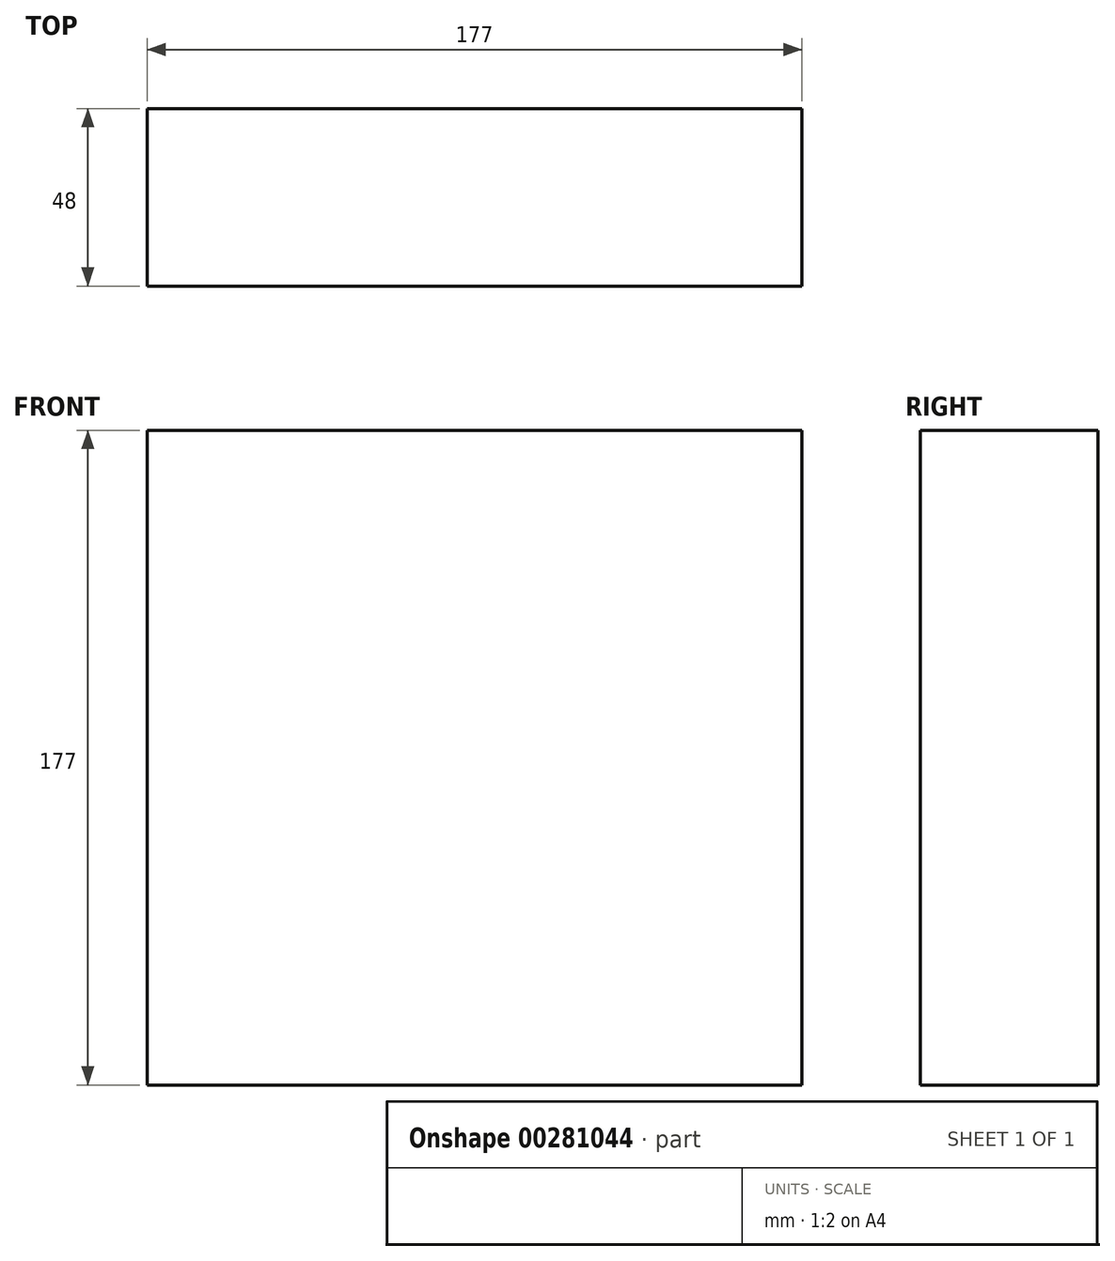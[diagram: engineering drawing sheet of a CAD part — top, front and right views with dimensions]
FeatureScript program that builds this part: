
annotation { "Feature Type Name" : "Feature", "Feature Type Description" : "" }
export const myFeature = defineFeature(function(context is Context, id is Id, definition is map)
    precondition{}
    {
        {
            var Q0;
            Q0=qCreatedBy(makeId("Front.planeOp"),FACE);
            var sketch = newSketch(context, id + "F0", { "sketchPlane" : qUnion([Q0])});
            skLineSegment(sketch, "E0.bottom", {"start": v(88.5, -88.5) * mm, "end": v(-88.5, -88.5) * mm});
            skLineSegment(sketch, "E0.top", {"start": v(88.5, 88.5) * mm, "end": v(-88.5, 88.5) * mm});
            skLineSegment(sketch, "E0.left", {"start": v(88.5, -88.5) * mm, "end": v(88.5, 88.5) * mm});
            skLineSegment(sketch, "E0.right", {"start": v(-88.5, -88.5) * mm, "end": v(-88.5, 88.5) * mm});
            skPoint(sketch, "E0.middle", {"position": v(0, 0) * mm});
            skSolve(sketch);
        }
        {
            var Q0;
            Q0 = qSketchRegion(id + "F0", true);
            extrude(context, id + "F1", {"entities" : qUnion([Q0]), "depth" : 48 * mm});
        }
        {
            var Q0;
            Q0=makeQuery(id+"F0.imprint","IMPRINT",FACE,{"disambiguationData":[TD([[makeQuery(id+"F0.imprint","IMPRINT",EDGE,{"derivedFrom":sQuery(id+"F0.wireOp",EDGE,"E0.bottom")}),-1.0]])]});
            extrude(context, id + "F2", {"entities" : qUnion([Q0]), "operationType" : NewBodyOperationType.ADD, "depth" : 25 * mm});
        }
    });
